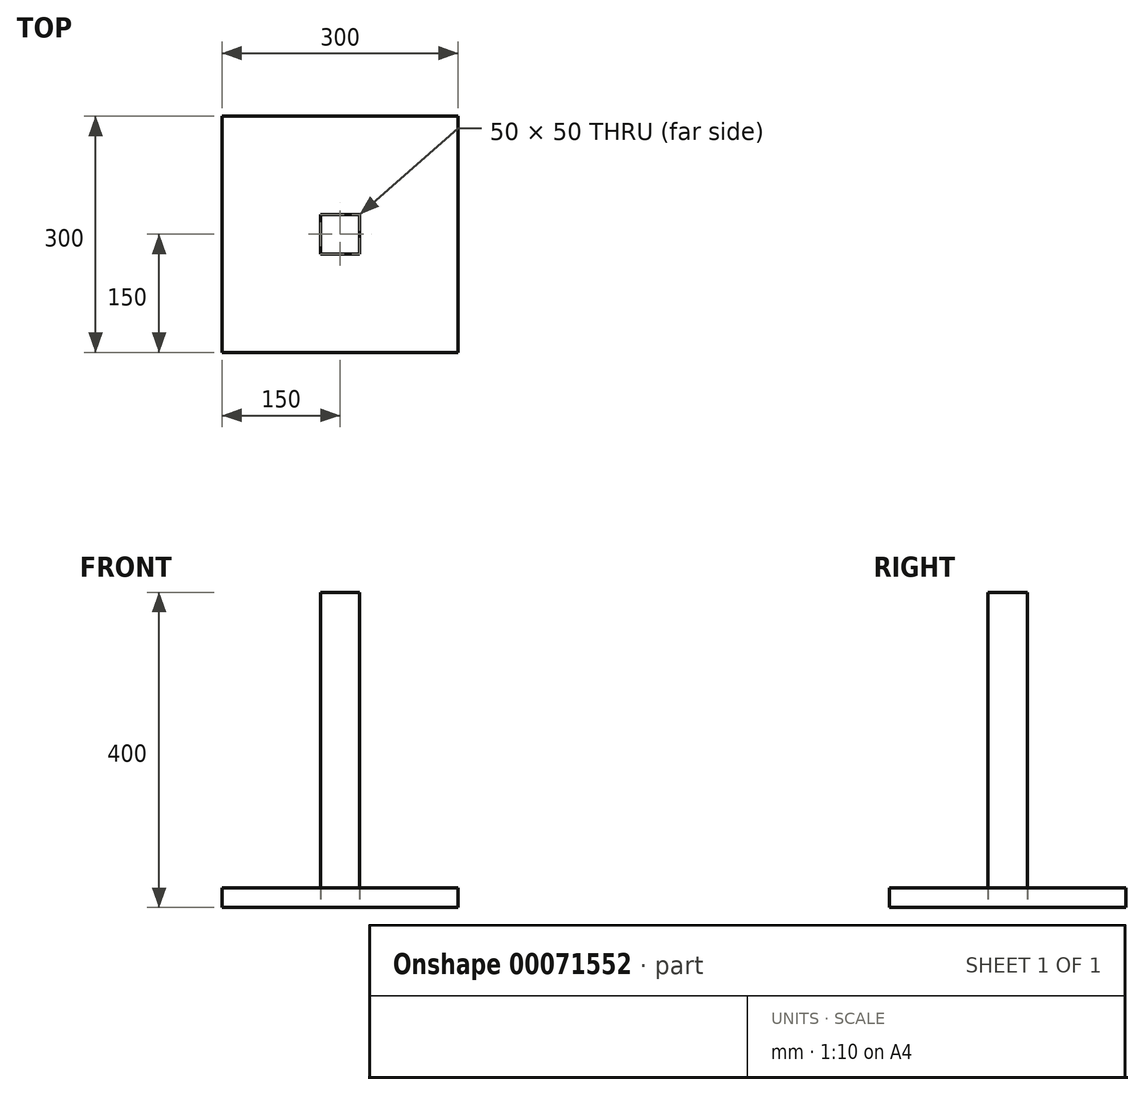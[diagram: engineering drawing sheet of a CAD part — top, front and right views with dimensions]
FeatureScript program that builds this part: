
annotation { "Feature Type Name" : "Feature", "Feature Type Description" : "" }
export const myFeature = defineFeature(function(context is Context, id is Id, definition is map)
    precondition{}
    {
        {
            var Q0;
            Q0=qCreatedBy(makeId("Top.planeOp"),FACE);
            var sketch = newSketch(context, id + "F0", { "sketchPlane" : qUnion([Q0])});
            skLineSegment(sketch, "E0.bottom", {"start": v(0, 0) * mm, "end": v(300, 0) * mm});
            skLineSegment(sketch, "E0.top", {"start": v(0, 300) * mm, "end": v(300, 300) * mm});
            skLineSegment(sketch, "E0.left", {"start": v(0, 0) * mm, "end": v(0, 300) * mm});
            skLineSegment(sketch, "E0.right", {"start": v(300, 0) * mm, "end": v(300, 300) * mm});
            skLineSegment(sketch, "E1.bottom", {"start": v(125, 125) * mm, "end": v(175, 125) * mm});
            skLineSegment(sketch, "E1.top", {"start": v(125, 175) * mm, "end": v(175, 175) * mm});
            skLineSegment(sketch, "E1.left", {"start": v(125, 125) * mm, "end": v(125, 175) * mm});
            skLineSegment(sketch, "E1.right", {"start": v(175, 125) * mm, "end": v(175, 175) * mm});
            skSolve(sketch);
        }
        {
            var Q0;
            Q0=makeQuery(id+"F0.imprint","IMPRINT",FACE,{"disambiguationData":[TD([[makeQuery(id+"F0.imprint","IMPRINT",EDGE,{"derivedFrom":sQuery(id+"F0.wireOp",EDGE,"E0.bottom")}),1.0]])]});
            extrude(context, id + "F1", {"entities" : qUnion([Q0]), "oppositeDirection" : true, "depth" : 25 * mm});
        }
        {
            var Q0;
            Q0=makeQuery(id+"F1.opExtrude","CAP_FACE",FACE,{"disambiguationData":[OSD([sQuery(id+"F0.wireOp",EDGE,"E0.bottom"),sQuery(id+"F0.wireOp",EDGE,"E0.top"),sQuery(id+"F0.wireOp",EDGE,"E0.left"),sQuery(id+"F0.wireOp",EDGE,"E0.right"),sQuery(id+"F0.wireOp",EDGE,"E1.bottom"),sQuery(id+"F0.wireOp",EDGE,"E1.top"),sQuery(id+"F0.wireOp",EDGE,"E1.left"),sQuery(id+"F0.wireOp",EDGE,"E1.right")])],"isStart":false});
            var sketch = newSketch(context, id + "F2", { "sketchPlane" : qUnion([Q0])});
            skLineSegment(sketch, "E2.0", {"start": v(125, -125) * mm, "end": v(125, -175) * mm});
            skLineSegment(sketch, "E3.0", {"start": v(125, -125) * mm, "end": v(175, -125) * mm});
            skLineSegment(sketch, "E4.0", {"start": v(175, -125) * mm, "end": v(175, -175) * mm});
            skLineSegment(sketch, "E5.0", {"start": v(125, -175) * mm, "end": v(175, -175) * mm});
            skSolve(sketch);
        }
        {
            var Q0;
            Q0=makeQuery(id+"F2.imprint","IMPRINT",FACE,{"disambiguationData":[TD([[makeQuery(id+"F2.imprint","IMPRINT",EDGE,{"derivedFrom":sQuery(id+"F2.wireOp",EDGE,"E2.0")}),1.0]])]});
            extrude(context, id + "F3", {"entities" : qUnion([Q0]), "oppositeDirection" : true, "depth" : 400 * mm});
        }
    });
